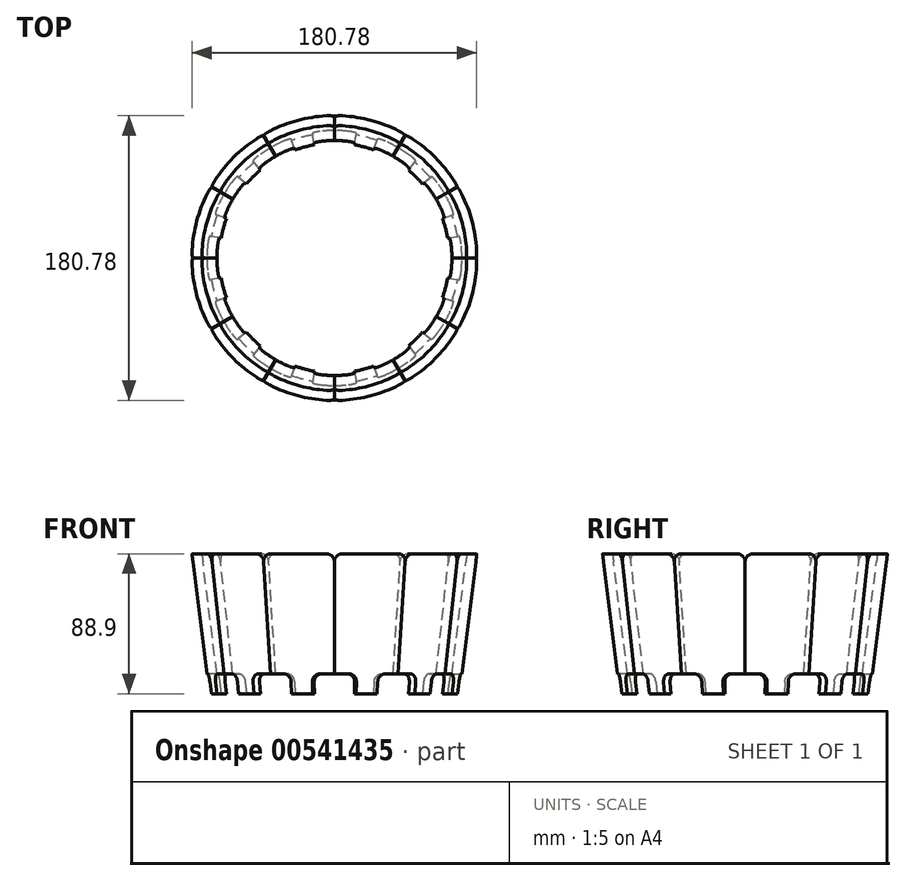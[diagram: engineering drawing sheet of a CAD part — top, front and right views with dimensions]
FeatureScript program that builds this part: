
annotation { "Feature Type Name" : "Feature", "Feature Type Description" : "" }
export const myFeature = defineFeature(function(context is Context, id is Id, definition is map)
    precondition{}
    {
        {
            var Q0;
            Q0=qCreatedBy(makeId("Front.planeOp"),FACE);
            var sketch = newSketch(context, id + "F0", { "sketchPlane" : qUnion([Q0])});
            skLineSegment(sketch, "E0", {"start": v(0, 0) * mm, "end": v(0, 76.2) * mm});
            skLineSegment(sketch, "E1", {"start": v(0, 76.2) * mm, "end": v(88.9, 76.2) * mm, "construction": true});
            skLineSegment(sketch, "E2", {"start": v(0, 0) * mm, "end": v(79.38, 0) * mm});
            skLineSegment(sketch, "E3", {"start": v(79.38, 0) * mm, "end": v(88.9, 76.2) * mm, "construction": true});
            skLineSegment(sketch, "E4", {"start": v(0, 76.2) * mm, "end": v(0, 88.9) * mm});
            skLineSegment(sketch, "E5", {"start": v(0, 88.9) * mm, "end": v(90.49, 88.9) * mm, "construction": true});
            skLineSegment(sketch, "E6", {"start": v(79.37, 0) * mm, "end": v(90.49, 88.9) * mm});
            skLineSegment(sketch, "E7", {"start": v(90.49, 88.9) * mm, "end": v(0, 88.9) * mm});
            skSolve(sketch);
        }
        {
            var Q0;
            Q0=makeQuery(id+"F0.imprint","IMPRINT",FACE,{"disambiguationData":[TD([[makeQuery(id+"F0.imprint","IMPRINT",EDGE,{"derivedFrom":sQuery(id+"F0.wireOp",EDGE,"E0")}),-1.0]])]});
            var Q1;
            Q1=sQuery(id+"F0.wireOp",EDGE,"E0");
            revolve(context, id + "F1", {"entities" : qUnion([Q0]), "axis" : qUnion([Q1]), "revolveType" : RevolveType.ONE_DIRECTION, "angle" : 30 * degree});
        }
        {
            var Q0;
            Q0=makeQuery(id+"F1.opRevolve","CAP_FACE",FACE,{"disambiguationData":[OSD([sQuery(id+"F0.wireOp",EDGE,"E0"),sQuery(id+"F0.wireOp",EDGE,"E2"),sQuery(id+"F0.wireOp",EDGE,"E4"),sQuery(id+"F0.wireOp",EDGE,"E6"),sQuery(id+"F0.wireOp",EDGE,"E7")])],"isStart":true});
            var sketch = newSketch(context, id + "F2", { "sketchPlane" : qUnion([Q0])});
            skLineSegment(sketch, "E8", {"start": v(0, 0) * mm, "end": v(73.03, 0) * mm});
            skLineSegment(sketch, "E9", {"start": v(0, 0) * mm, "end": v(0, 88.9) * mm});
            skLineSegment(sketch, "E10", {"start": v(0, 88.9) * mm, "end": v(84.14, 88.9) * mm});
            skLineSegment(sketch, "E11", {"start": v(84.14, 88.9) * mm, "end": v(73.03, 0) * mm});
            skSolve(sketch);
        }
        {
            var Q0;
            Q0=qSketchRegion(id+"F2",true);
            var Q1;
            Q1=sQuery(id+"F2.wireOp",EDGE,"E9");
            revolve(context, id + "F3", {"operationType" : NewBodyOperationType.REMOVE, "entities" : qUnion([Q0]), "axis" : qUnion([Q1]), "revolveType" : RevolveType.FULL, "oppositeDirection" : true});
        }
        {
            var Q0;
            Q0=makeQuery(id+"F1.opRevolve","SWEPT_FACE",FACE,{"disambiguationData":[OSD([sQuery(id+"F0.wireOp",EDGE,"E2")])]});
            var sketch = newSketch(context, id + "F4", { "sketchPlane" : qUnion([Q0])});
            skLineSegment(sketch, "E12", {"start": v(0, 0) * mm, "end": v(79.38, 0) * mm, "construction": true});
            skLineSegment(sketch, "E13", {"start": v(0, 0) * mm, "end": v(68.74, -39.69) * mm});
            skLineSegment(sketch, "E14", {"start": v(0, 0) * mm, "end": v(74.59, -27.15) * mm});
            skLineSegment(sketch, "E15", {"start": v(74.59, -27.15) * mm, "end": v(85.9, -31.26) * mm});
            skLineSegment(sketch, "E16", {"start": v(68.74, -39.69) * mm, "end": v(79.17, -45.7) * mm});
            skArc(sketch, "E17", {"start": v(79.17, -45.7) * mm, "mid": v(87.8, -40.94) * mm, "end": v(85.9, -31.26) * mm});
            skSolve(sketch);
        }
        {
            var Q0;
            {var subQ0=sQuery(id+"F4.wireOp",EDGE,"E15");Q0=makeQuery(id+"F4.imprint","IMPRINT",FACE,{"disambiguationData":[TD([[makeQuery(id+"F4.imprint","IMPRINT",EDGE,{"derivedFrom":subQ0}),-1.0]])]});}
            var Q1;
            {var subQ0=sQuery(id+"F4.wireOp",EDGE,"E13");var subQ3=sQuery(id+"F4.wireOp",EDGE,"E14");var subQ4=makeQuery(id+"F4.imprint","INTERSECT",VERTEX,{"derivedFrom":[subQ0,subQ3]});Q1=makeQuery(id+"F4.imprint","IMPRINT",FACE,{"disambiguationData":[TD([[makeQuery(id+"F4.imprint","IMPRINT",EDGE,{"disambiguationData":[TD([[subQ4,-1.0]])],"derivedFrom":subQ0}),1.0]])]});}
            var Q2;
            {var subQ0=sQuery(id+"F4.wireOp",EDGE,"E13");var subQ1=sQuery(id+"F0.wireOp",EDGE,"E2");var subQ2=makeQuery(id+"F1.opRevolve","SWEPT_EDGE",EDGE,{"disambiguationData":[OSD([subQ1,sQuery(id+"F0.wireOp",EDGE,"E6")])]});var subQ3=makeQuery(id+"F4.imprint","INTERSECT",VERTEX,{"derivedFrom":[subQ2,subQ0,sQuery(id+"F4.wireOp",EDGE,"E16")]});Q2=makeQuery(id+"F4.imprint","IMPRINT",FACE,{"disambiguationData":[TD([[makeQuery(id+"F4.imprint","IMPRINT",EDGE,{"disambiguationData":[TD([[subQ3,1.0]])],"derivedFrom":subQ0}),1.0]])]});}
            extrude(context, id + "F5", {"entities" : qUnion([Q0, Q1, Q2]), "operationType" : NewBodyOperationType.REMOVE, "oppositeDirection" : true, "depth" : 12.7 * mm, "offsetDistance" : 25.4 * mm});
        }
        {
            var Q0;
            Q0=makeQuery(id+"F1.opRevolve","SWEPT_FACE",FACE,{"disambiguationData":[OSD([sQuery(id+"F0.wireOp",EDGE,"E2")])]});
            var sketch = newSketch(context, id + "F6", { "sketchPlane" : qUnion([Q0])});
            skLineSegment(sketch, "E18", {"start": v(0, 0) * mm, "end": v(85.05, -15) * mm});
            skLineSegment(sketch, "E19", {"start": v(0, 0) * mm, "end": v(86.36, 0) * mm});
            skArc(sketch, "E20", {"start": v(85.05, -15) * mm, "mid": v(87.92, -7.7) * mm, "end": v(86.36, 0) * mm});
            skSolve(sketch);
        }
        {
            var Q0;
            {var subQ0=sQuery(id+"F6.wireOp",EDGE,"E20");Q0=makeQuery(id+"F6.imprint","IMPRINT",FACE,{"disambiguationData":[TD([[makeQuery(id+"F6.imprint","IMPRINT",EDGE,{"derivedFrom":subQ0}),1.0]])]});}
            var Q1;
            {var subQ0=sQuery(id+"F6.wireOp",EDGE,"E18");var subQ1=sQuery(id+"F0.wireOp",EDGE,"E2");var subQ4=makeQuery(id+"F1.opRevolve","SWEPT_EDGE",EDGE,{"disambiguationData":[OSD([subQ1,sQuery(id+"F0.wireOp",EDGE,"E6")])]});var subQ5=makeQuery(id+"F6.imprint","INTERSECT",VERTEX,{"derivedFrom":[subQ4,subQ0]});Q1=makeQuery(id+"F6.imprint","IMPRINT",FACE,{"disambiguationData":[TD([[makeQuery(id+"F6.imprint","IMPRINT",EDGE,{"disambiguationData":[TD([[subQ5,1.0]])],"derivedFrom":subQ0}),1.0]])]});}
            var Q2;
            {var subQ0=sQuery(id+"F6.wireOp",EDGE,"E19");var subQ1=sQuery(id+"F6.wireOp",EDGE,"E18");var subQ2=makeQuery(id+"F6.imprint","INTERSECT",VERTEX,{"derivedFrom":[subQ1,subQ0]});Q2=makeQuery(id+"F6.imprint","IMPRINT",FACE,{"disambiguationData":[TD([[makeQuery(id+"F6.imprint","IMPRINT",EDGE,{"disambiguationData":[TD([[subQ2,-1.0]])],"derivedFrom":subQ1}),1.0]])]});}
            extrude(context, id + "F7", {"entities" : qUnion([Q0, Q1, Q2]), "operationType" : NewBodyOperationType.REMOVE, "oppositeDirection" : true, "depth" : 12.7 * mm, "offsetDistance" : 25.4 * mm});
        }
        {
            var Q0;
            Q0=makeQuery(id+"F5.boolean.opBoolean","COPY",EDGE,{"derivedFrom":makeQuery(id+"F5.opExtrude","CAP_EDGE",EDGE,{"disambiguationData":[OSD([sQuery(id+"F4.wireOp",EDGE,"E14"),sQuery(id+"F4.wireOp",EDGE,"E15")])],"isStart":false})});
            var Q1;
            Q1=makeQuery(id+"F5.boolean.opBoolean","COPY",EDGE,{"derivedFrom":makeQuery(id+"F5.opExtrude","CAP_EDGE",EDGE,{"disambiguationData":[OSD([sQuery(id+"F4.wireOp",EDGE,"E14"),sQuery(id+"F4.wireOp",EDGE,"E15")])],"isStart":true})});
            var Q2;
            Q2=makeQuery(id+"F7.boolean.opBoolean","COPY",EDGE,{"derivedFrom":makeQuery(id+"F7.opExtrude","CAP_EDGE",EDGE,{"disambiguationData":[OSD([sQuery(id+"F6.wireOp",EDGE,"E18")])],"isStart":true})});
            var Q3;
            Q3=makeQuery(id+"F7.boolean.opBoolean","COPY",EDGE,{"derivedFrom":makeQuery(id+"F7.opExtrude","CAP_EDGE",EDGE,{"disambiguationData":[OSD([sQuery(id+"F6.wireOp",EDGE,"E18")])],"isStart":false})});
            var Q4;
            Q4=makeQuery(id+"F7.boolean.opBoolean","COPY",EDGE,{"derivedFrom":makeQuery(id+"F7.opExtrude","CAP_EDGE",EDGE,{"disambiguationData":[OSD([sQuery(id+"F6.wireOp",EDGE,"E19")])],"isStart":false})});
            var Q5;
            Q5=makeQuery(id+"F1.opRevolve","CAP_EDGE",EDGE,{"disambiguationData":[OSD([sQuery(id+"F0.wireOp",EDGE,"E7")])],"isStart":true});
            var Q6;
            Q6=makeQuery(id+"F1.opRevolve","CAP_EDGE",EDGE,{"disambiguationData":[OSD([sQuery(id+"F0.wireOp",EDGE,"E7")])],"isStart":false});
            var Q7;
            Q7=makeQuery(id+"F5.boolean.opBoolean","COPY",EDGE,{"derivedFrom":makeQuery(id+"F5.opExtrude","CAP_EDGE",EDGE,{"disambiguationData":[OSD([sQuery(id+"F4.wireOp",EDGE,"E13"),sQuery(id+"F4.wireOp",EDGE,"E16")])],"isStart":false})});
            fillet(context, id + "F8", {"entities" : qUnion([Q0, Q1, Q2, Q3, Q4, Q5, Q6, Q7]), "radius" : 5.08 * mm, "tangentPropagation" : true, "allowEdgeOverflow" : false});
        }
        {
            var Q0;
            Q0=qCreatedBy(makeId("Front.planeOp"),FACE);
            var sketch = newSketch(context, id + "F9", { "sketchPlane" : qUnion([Q0])});
            skLineSegment(sketch, "E21", {"start": v(0, 0) * mm, "end": v(0, 44.25) * mm, "construction": true});
            skSolve(sketch);
        }
        {
            var Q0;
            Q0=makeQuery(id+"F1.opRevolve","SWEPT_BODY",BODY,{"disambiguationData":[OSD([sQuery(id+"F0.wireOp",EDGE,"E0"),sQuery(id+"F0.wireOp",EDGE,"E2"),sQuery(id+"F0.wireOp",EDGE,"E4"),sQuery(id+"F0.wireOp",EDGE,"E6"),sQuery(id+"F0.wireOp",EDGE,"E7")])]});
            var Q1;
            Q1=sQuery(id+"F9.wireOp",EDGE,"E21");
            circularPattern(context, id + "F10", {"entities" : qUnion([Q0]), "axis" : qUnion([Q1]), "angle" : 360 * degree, "instanceCount" : 12, "equalSpace" : true});
        }
    });
